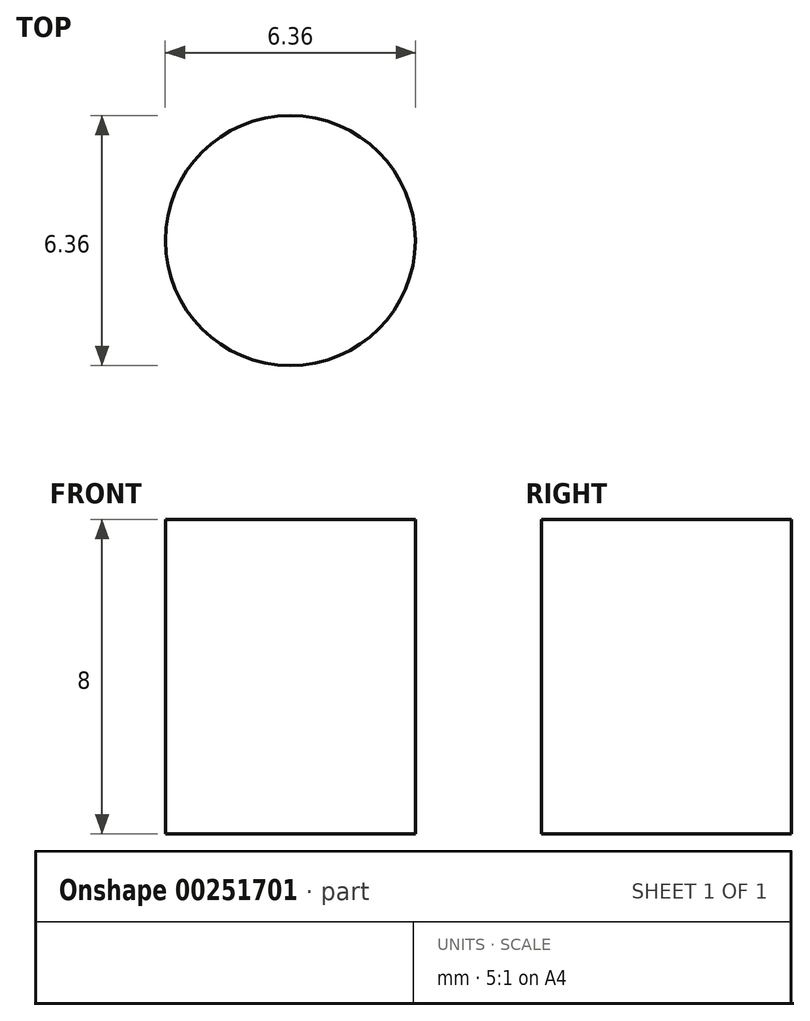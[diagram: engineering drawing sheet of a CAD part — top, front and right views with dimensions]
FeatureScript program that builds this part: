
annotation { "Feature Type Name" : "Feature", "Feature Type Description" : "" }
export const myFeature = defineFeature(function(context is Context, id is Id, definition is map)
    precondition{}
    {
        {
            var Q0;
            Q0=qCreatedBy(makeId("Top.planeOp"),FACE);
            var sketch = newSketch(context, id + "F0", { "sketchPlane" : qUnion([Q0])});
            skCircle(sketch, "E0", {"center": v(0, 0) * mm, "radius": 3.18 * mm});
            skSolve(sketch);
        }
        {
            var Q0;
            Q0 = qSketchRegion(id + "F0", true);
            extrude(context, id + "F1", {"entities" : qUnion([Q0]), "endBound" : BoundingType.SYMMETRIC, "depth" : 8 * mm});
        }
    });
